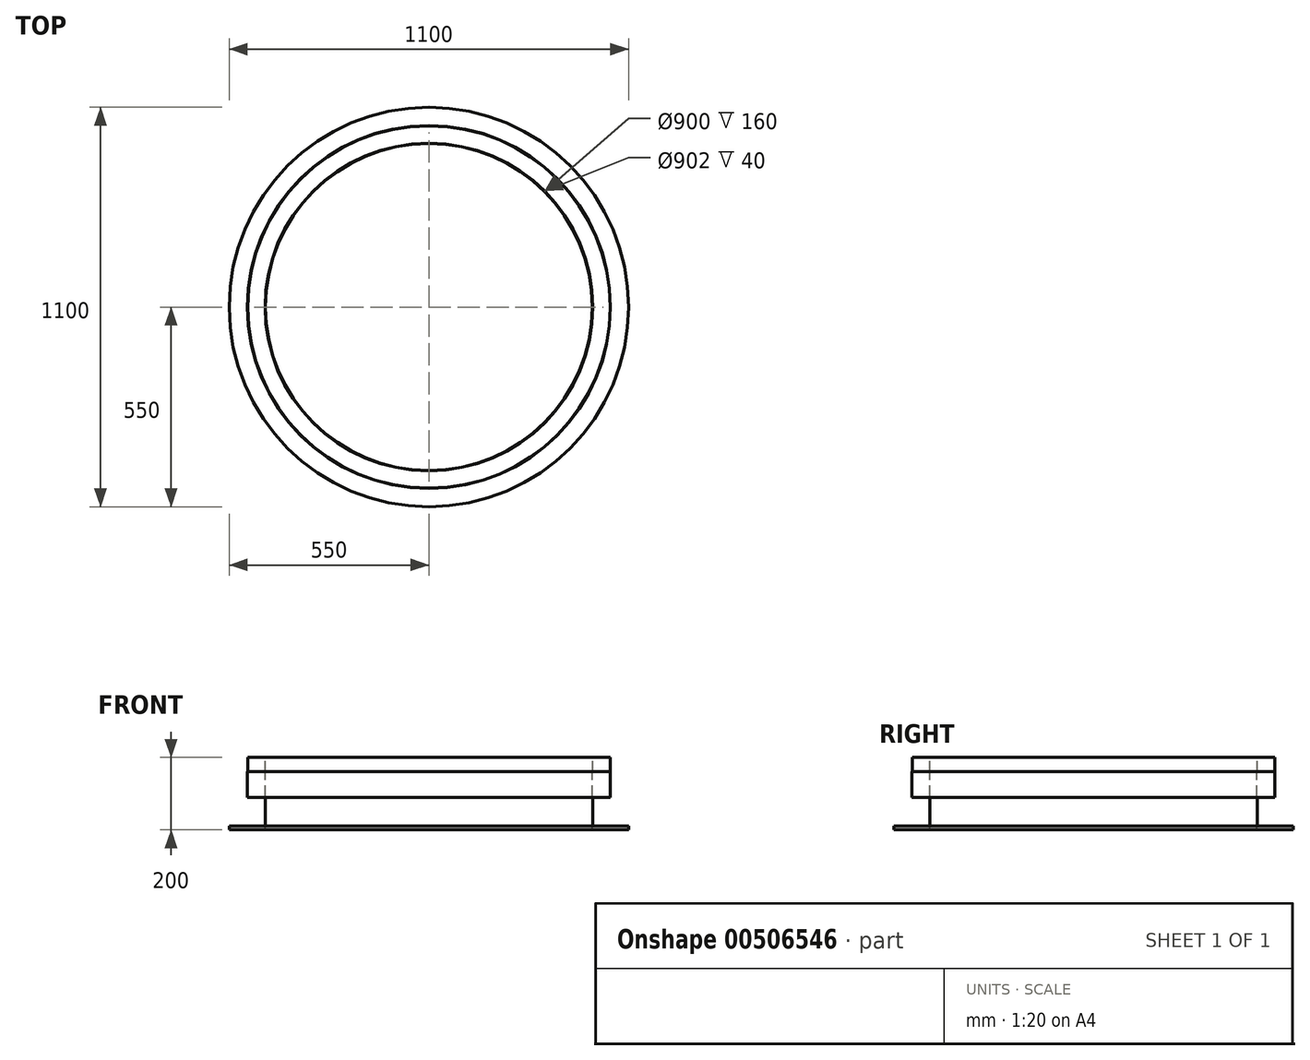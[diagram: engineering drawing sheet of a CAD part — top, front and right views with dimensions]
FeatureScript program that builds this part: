
annotation { "Feature Type Name" : "Feature", "Feature Type Description" : "" }
export const myFeature = defineFeature(function(context is Context, id is Id, definition is map)
    precondition{}
    {
        {
            var Q0;
            Q0=qCreatedBy(makeId("Front.planeOp"),FACE);
            var sketch = newSketch(context, id + "F0", { "sketchPlane" : qUnion([Q0])});
            skLineSegment(sketch, "E0", {"start": v(0, 710.75) * mm, "end": v(0, -704.58) * mm, "construction": true});
            skLineSegment(sketch, "E1", {"start": v(-450, 300.65) * mm, "end": v(-450, 460.65) * mm});
            skLineSegment(sketch, "E2", {"start": v(-450, 460.65) * mm, "end": v(-451, 460.65) * mm});
            skLineSegment(sketch, "E3", {"start": v(-499, 460.65) * mm, "end": v(-500, 460.65) * mm});
            skLineSegment(sketch, "E4", {"start": v(-500, 460.65) * mm, "end": v(-500, 390.65) * mm});
            skLineSegment(sketch, "E5", {"start": v(-500, 390.65) * mm, "end": v(-451, 390.65) * mm});
            skLineSegment(sketch, "E6", {"start": v(-451, 390.65) * mm, "end": v(-451, 310.65) * mm});
            skLineSegment(sketch, "E7", {"start": v(-451, 310.65) * mm, "end": v(-550, 310.65) * mm});
            skLineSegment(sketch, "E8", {"start": v(-550, 310.65) * mm, "end": v(-550, 300.65) * mm});
            skLineSegment(sketch, "E9", {"start": v(-550, 300.65) * mm, "end": v(-450, 300.65) * mm});
            skLineSegment(sketch, "E10", {"start": v(-499, 500.65) * mm, "end": v(-499, 460.65) * mm});
            skLineSegment(sketch, "E11", {"start": v(-499, 500.65) * mm, "end": v(-451, 500.65) * mm});
            skLineSegment(sketch, "E12", {"start": v(-451, 460.65) * mm, "end": v(-451, 500.65) * mm});
            skSolve(sketch);
        }
        {
            var Q0;
            Q0=qSketchRegion(id+"F0",true);
            var Q1;
            Q1=sQuery(id+"F0.wireOp",EDGE,"E0");
            revolve(context, id + "F1", {"entities" : qUnion([Q0]), "axis" : qUnion([Q1]), "revolveType" : RevolveType.FULL});
        }
    });
